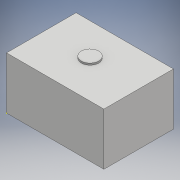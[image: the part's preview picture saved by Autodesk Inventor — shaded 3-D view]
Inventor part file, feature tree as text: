
AUTODESK INVENTOR PART (.ipt)
format: ipt  version: 2018 (Build 220112000, 112)  size: 92,160 bytes
history: native  units: mm
features: sketch x3, extrude x2
ambient origin geometry x8: Origin, YZ Plane, XZ Plane, XY Plane, X Axis, Y Axis, Z Axis, Center Point
bodies: Solid1 (feature_tree)
feature tree (5):
  sketch  "Sketch2"  dims[d0=280.0mm d1=200.0mm]
  extrude  "Extrusion1"  Depth=200.0mm
  extrude  "Extrusion2"  Depth=150.0mm
  sketch  "Sketch3"  dims[d2=150.0mm d3=0.0mm d4=50.0mm]
  sketch  "Sketch4"  dims[d5=5.0mm d6=0.0mm]
